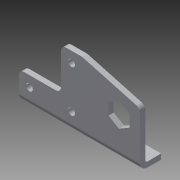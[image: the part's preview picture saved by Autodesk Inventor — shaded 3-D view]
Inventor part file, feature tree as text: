
AUTODESK INVENTOR PART (.ipt)
format: ipt  version: 2014 (Build 180170000, 170)  size: 134,656 bytes
history: native  units: in
note: dims shown in document units (in); Inventor stores cm internally (conversion verified against a paired STEP export)
features: sheet_metal_op x4, sketch x2, other x2, fillet x1
ambient origin geometry x8: Origin, YZ Plane, XZ Plane, XY Plane, X Axis, Y Axis, Z Axis, Center Point
bodies: Solid1 (feature_tree)
feature tree (9):
  sheet_metal_op  "Face1"
  sheet_metal_op  "Flange1"
  fillet  "Fillet2"  Radius=0.5in
  sketch  "Sketch1"  dims[d1=1.0in]
  other  "Plate1"
  sketch  "Sketch2"  dims[d2=1.0in d3=0.5in d4=2.875in d5=0.5in d6=0.75in d7=0.5in d8=90.0deg d9=1.125in d10=0.163in d11=0.25in d12=0.25in d13=0.7874in d15=1.0in d16=0.3937in d18=1.0in d20=0.7874in d22=1.0in d23=0.3937in d25=1.0in d27=0.125in d29=0.125in d30=0.0625in d31=0.25in d32=0.125in d33=0.5in d34=90.0deg d35=0.05in d36=0.5in d37=0.125in d38=0.125in d39=0.125in]
  other  "Plate2"
  sheet_metal_op  "Bend1"
  sheet_metal_op  "Corner1"
